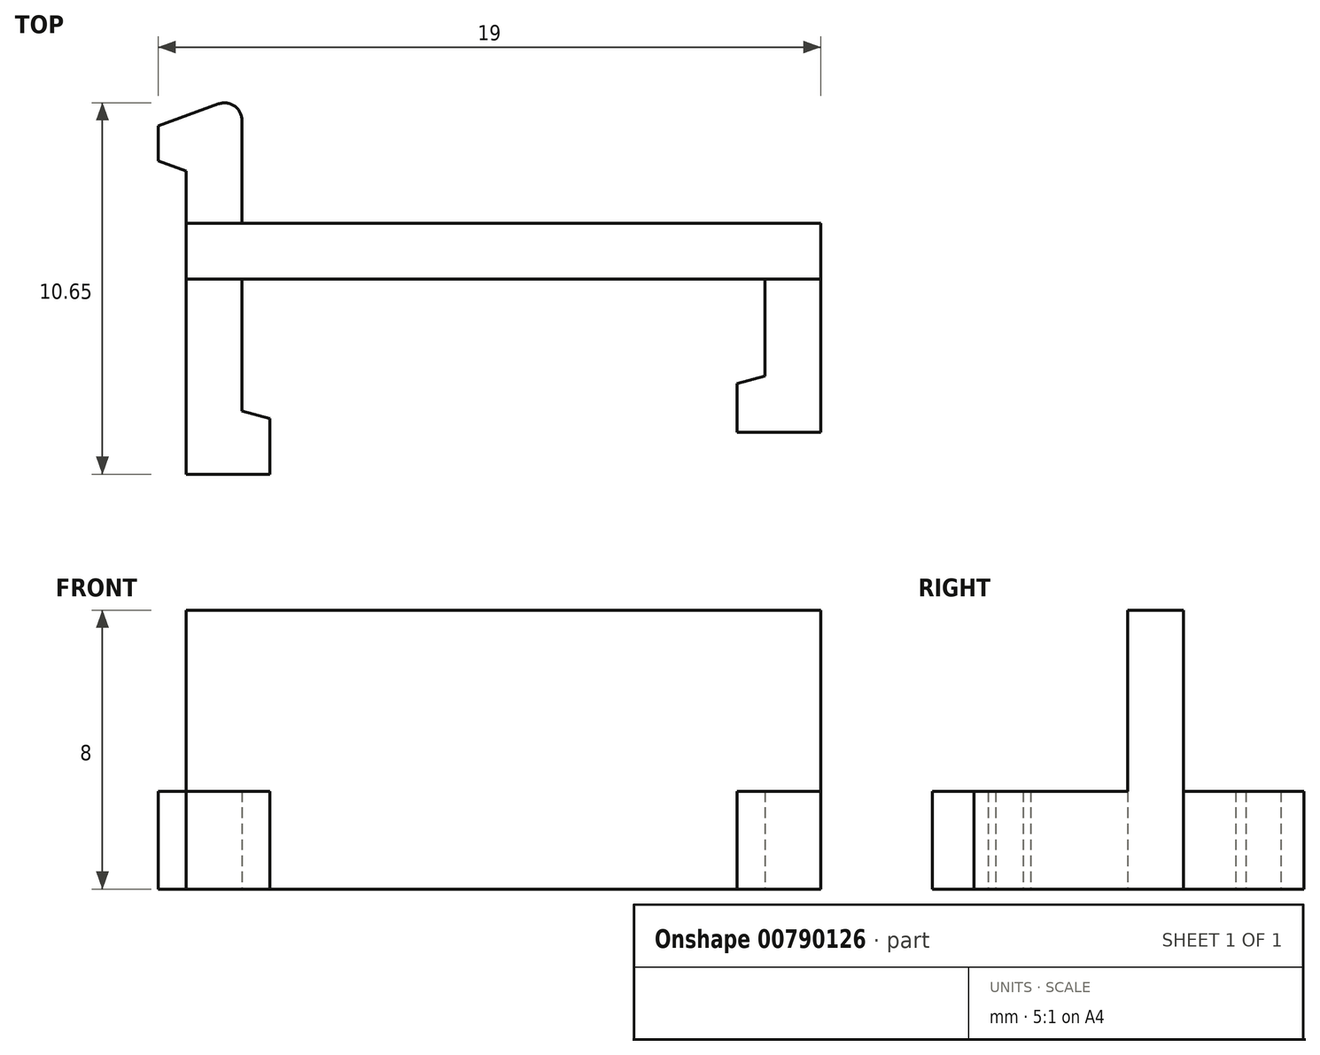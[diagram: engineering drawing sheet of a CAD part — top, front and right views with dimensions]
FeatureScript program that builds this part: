
annotation { "Feature Type Name" : "Feature", "Feature Type Description" : "" }
export const myFeature = defineFeature(function(context is Context, id is Id, definition is map)
    precondition{}
    {
        {
            var Q0;
            Q0=qCreatedBy(makeId("Front.planeOp"),FACE);
            var sketch = newSketch(context, id + "F0", { "sketchPlane" : qUnion([Q0])});
            skLineSegment(sketch, "E0.bottom", {"start": v(-9.1, 4) * mm, "end": v(9.1, 4) * mm});
            skLineSegment(sketch, "E0.top", {"start": v(-9.1, -4) * mm, "end": v(9.1, -4) * mm});
            skLineSegment(sketch, "E0.left", {"start": v(-9.1, 4) * mm, "end": v(-9.1, -4) * mm});
            skLineSegment(sketch, "E0.right", {"start": v(9.1, 4) * mm, "end": v(9.1, -4) * mm});
            skPoint(sketch, "E0.middle", {"position": v(0, 0) * mm});
            skSolve(sketch);
        }
        {
            var Q0;
            Q0=makeQuery(id+"F0.imprint","IMPRINT",FACE,{"disambiguationData":[TD([[makeQuery(id+"F0.imprint","IMPRINT",EDGE,{"derivedFrom":sQuery(id+"F0.wireOp",EDGE,"E0.bottom")}),-1.0]])]});
            extrude(context, id + "F1", {"entities" : qUnion([Q0]), "depth" : 1.6 * mm, "offsetDistance" : 25 * mm});
        }
        {
            var Q0;
            Q0=makeQuery(id+"F1.opExtrude","SWEPT_FACE",FACE,{"disambiguationData":[OSD([sQuery(id+"F0.wireOp",EDGE,"E0.top")])]});
            var sketch = newSketch(context, id + "F2", { "sketchPlane" : qUnion([Q0])});
            skLineSegment(sketch, "E1", {"start": v(-9.1, 1.6) * mm, "end": v(-9.1, 7.2) * mm});
            skLineSegment(sketch, "E2", {"start": v(-9.1, 7.2) * mm, "end": v(-6.7, 7.2) * mm});
            skLineSegment(sketch, "E3", {"start": v(-6.7, 7.2) * mm, "end": v(-6.7, 5.6) * mm});
            skLineSegment(sketch, "E4", {"start": v(-6.7, 5.6) * mm, "end": v(-7.5, 5.39) * mm});
            skLineSegment(sketch, "E5", {"start": v(-7.5, 5.39) * mm, "end": v(-7.5, 1.6) * mm});
            skLineSegment(sketch, "E6", {"start": v(-7.5, 1.6) * mm, "end": v(-9.1, 1.6) * mm});
            skLineSegment(sketch, "E7.MirrorCS", {"start": v(7.5, 1.6) * mm, "end": v(9.1, 1.6) * mm});
            skLineSegment(sketch, "E8.MirrorCS", {"start": v(9.1, 1.6) * mm, "end": v(9.1, 6) * mm});
            skLineSegment(sketch, "E9.MirrorCS", {"start": v(7.5, 4.39) * mm, "end": v(7.5, 1.6) * mm});
            skLineSegment(sketch, "E10", {"start": v(6.7, 6) * mm, "end": v(6.7, 4.6) * mm});
            skLineSegment(sketch, "E11", {"start": v(6.7, 4.6) * mm, "end": v(7.5, 4.39) * mm});
            skLineSegment(sketch, "E12", {"start": v(6.7, 6) * mm, "end": v(9.1, 6) * mm});
            skLineSegment(sketch, "E13", {"start": v(-9.1, 0) * mm, "end": v(-9.1, -1.5) * mm});
            skLineSegment(sketch, "E14", {"start": v(-7.5, -2.95) * mm, "end": v(-7.5, 0) * mm});
            skLineSegment(sketch, "E15", {"start": v(-9.1, -1.5) * mm, "end": v(-9.9, -1.8) * mm});
            skLineSegment(sketch, "E16", {"start": v(-9.9, -1.8) * mm, "end": v(-9.9, -2.8) * mm});
            skLineSegment(sketch, "E17", {"start": v(-9.9, -2.8) * mm, "end": v(-8.17, -3.42) * mm});
            skPoint(sketch, "E18.visualSharp", {"position": v(-7.5, -3.66) * mm});
            skArc(sketch, "E18.filletArc", {"start": v(-8.17, -3.42) * mm, "mid": v(-7.71, -3.36) * mm, "end": v(-7.5, -2.95) * mm});
            skArc(sketch, "E19.MirrorCS", {"start": v(8.17, -3.42) * mm, "mid": v(7.71, -3.36) * mm, "end": v(7.5, -2.95) * mm});
            skLineSegment(sketch, "E20.MirrorCS", {"start": v(9.1, -1.5) * mm, "end": v(9.9, -1.8) * mm});
            skLineSegment(sketch, "E21.MirrorCS", {"start": v(9.1, 0) * mm, "end": v(9.1, -1.5) * mm});
            skLineSegment(sketch, "E22.MirrorCS", {"start": v(9.9, -1.8) * mm, "end": v(9.9, -2.8) * mm});
            skPoint(sketch, "E23.MirrorP", {"position": v(7.5, -3.66) * mm});
            skLineSegment(sketch, "E24.MirrorCS", {"start": v(9.9, -2.8) * mm, "end": v(8.17, -3.42) * mm});
            skLineSegment(sketch, "E25.MirrorCS", {"start": v(7.5, -2.95) * mm, "end": v(7.5, 0) * mm});
            skSolve(sketch);
        }
        {
            var Q0;
            Q0=makeQuery(id+"F2.imprint","IMPRINT",FACE,{"disambiguationData":[TD([[makeQuery(id+"F2.imprint","IMPRINT",EDGE,{"derivedFrom":sQuery(id+"F2.wireOp",EDGE,"E1")}),-1.0]])]});
            var Q1;
            Q1=makeQuery(id+"F2.imprint","IMPRINT",FACE,{"disambiguationData":[TD([[makeQuery(id+"F2.imprint","IMPRINT",EDGE,{"derivedFrom":sQuery(id+"F2.wireOp",EDGE,"E7.MirrorCS")}),1.0]])]});
            var Q2;
            {var subQ1=sQuery(id+"F2.wireOp",EDGE,"E13");Q2=makeQuery(id+"F2.imprint","IMPRINT",FACE,{"disambiguationData":[TD([[makeQuery(id+"F2.imprint","IMPRINT",EDGE,{"derivedFrom":subQ1}),1.0]])]});}
            var Q3;
            Q3=makeQuery(id+"F2.imprint","IMPRINT",FACE,{"disambiguationData":[TD([[makeQuery(id+"F2.imprint","IMPRINT",EDGE,{"derivedFrom":sQuery(id+"F2.wireOp",EDGE,"E19.MirrorCS")}),-1.0]])]});
            extrude(context, id + "F3", {"entities" : qUnion([Q0, Q1, Q2, Q3]), "operationType" : NewBodyOperationType.ADD, "oppositeDirection" : true, "depth" : 2.8 * mm, "offsetDistance" : 25 * mm});
        }
    });
